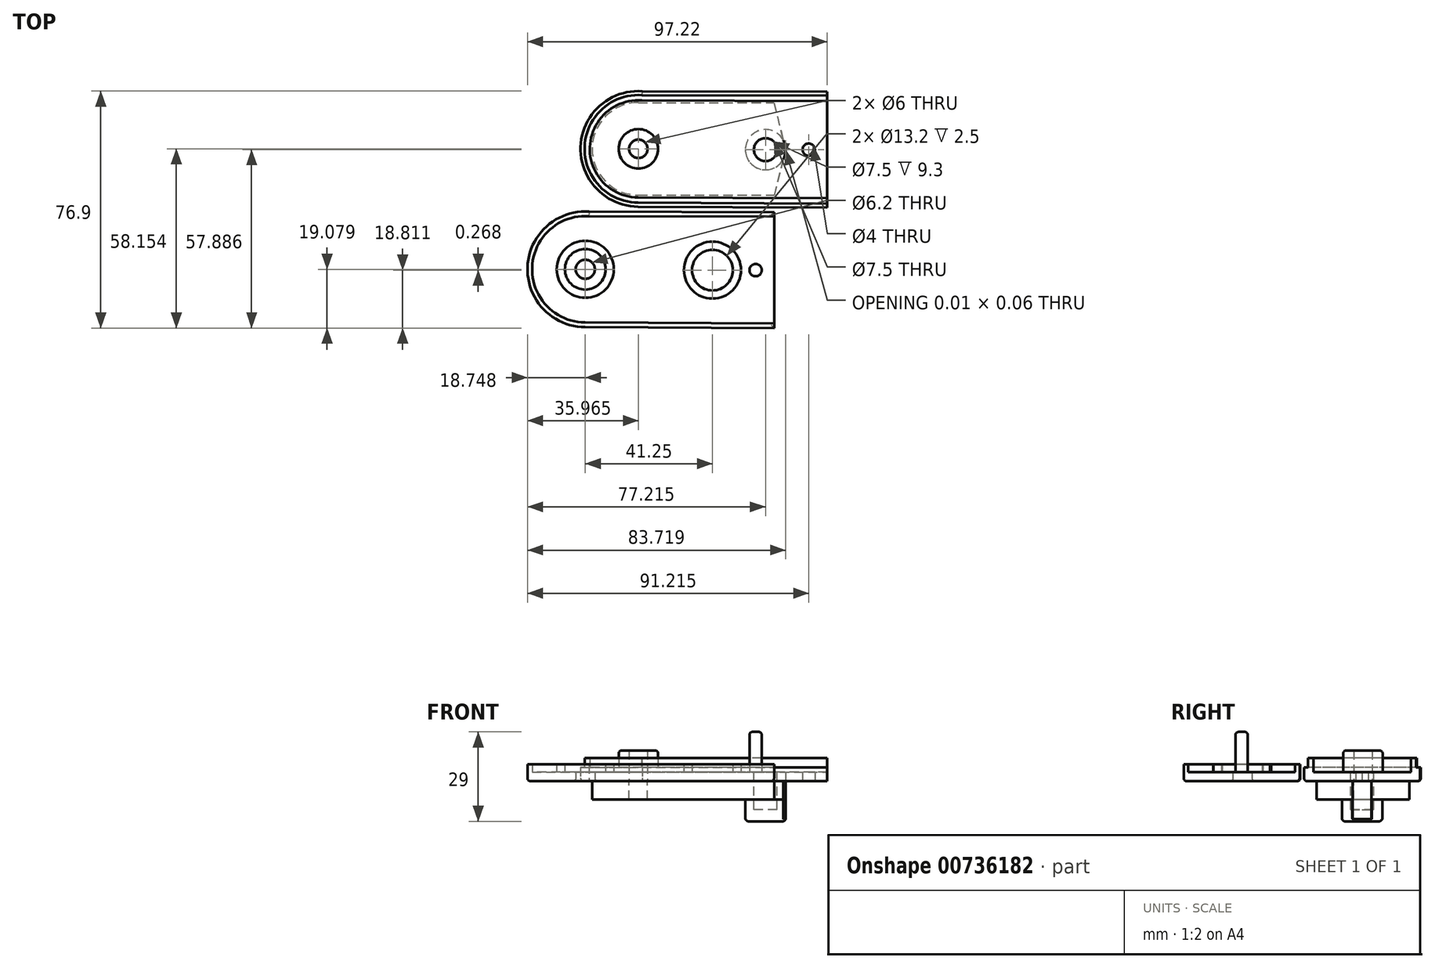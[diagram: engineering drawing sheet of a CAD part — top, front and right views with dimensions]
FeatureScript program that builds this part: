
annotation { "Feature Type Name" : "Feature", "Feature Type Description" : "" }
export const myFeature = defineFeature(function(context is Context, id is Id, definition is map)
    precondition{}
    {
        {
            var Q0;
            Q0=qCreatedBy(makeId("Top.planeOp"),FACE);
            var sketch = newSketch(context, id + "F0", { "sketchPlane" : qUnion([Q0])});
            skArc(sketch, "E0", {"start": v(-10, 58.38) * mm, "mid": v(-29.96, 40.34) * mm, "end": v(-11.32, 20.92) * mm});
            skCircle(sketch, "E1", {"center": v(-11.22, 39.67) * mm, "radius": 6.4 * mm});
            skCircle(sketch, "E2", {"center": v(-11.22, 39.67) * mm, "radius": 3 * mm});
            skLineSegment(sketch, "E3", {"start": v(50.03, 58.21) * mm, "end": v(50.03, 20.6) * mm});
            skLineSegment(sketch, "E4", {"start": v(50.03, 20.6) * mm, "end": v(-11.32, 20.92) * mm});
            skLineSegment(sketch, "E5", {"start": v(-10, 58.38) * mm, "end": v(50.03, 58.21) * mm});
            skCircle(sketch, "E6", {"center": v(30.03, 39.4) * mm, "radius": 4 * mm});
            skCircle(sketch, "E7", {"center": v(44.03, 39.4) * mm, "radius": 2 * mm});
            skArc(sketch, "E8", {"start": v(31.89, 45.64) * mm, "mid": v(23.52, 39.41) * mm, "end": v(31.88, 33.17) * mm});
            skArc(sketch, "E9", {"start": v(-11.27, 54.67) * mm, "mid": v(-26.22, 39.67) * mm, "end": v(-11.27, 24.67) * mm});
            skLineSegment(sketch, "E10.bottom", {"start": v(-11.27, 54.67) * mm, "end": v(32.73, 54.67) * mm});
            skLineSegment(sketch, "E10.top", {"start": v(-11.27, 24.67) * mm, "end": v(32.84, 24.67) * mm});
            skLineSegment(sketch, "E11.0", {"start": v(-10.1, 55.38) * mm, "end": v(50.02, 55.21) * mm});
            skArc(sketch, "E11.1", {"start": v(-10.1, 55.38) * mm, "mid": v(-26.96, 40.28) * mm, "end": v(-11.3, 23.92) * mm});
            skLineSegment(sketch, "E11.2", {"start": v(50.04, 23.6) * mm, "end": v(-11.3, 23.92) * mm});
            skLineSegment(sketch, "E12", {"start": v(32.73, 54.67) * mm, "end": v(35.78, 42.43) * mm});
            skLineSegment(sketch, "E13", {"start": v(36.53, 39.4) * mm, "end": v(36.53, 39.37) * mm});
            skLineSegment(sketch, "E14.0", {"start": v(-11.2, 27.67) * mm, "end": v(30.5, 27.67) * mm});
            skArc(sketch, "E14.1", {"start": v(-11.27, 51.67) * mm, "mid": v(-23.22, 39.64) * mm, "end": v(-11.2, 27.67) * mm});
            skLineSegment(sketch, "E14.2", {"start": v(-11.27, 51.67) * mm, "end": v(30.38, 51.67) * mm});
            skLineSegment(sketch, "E14.3", {"start": v(30.38, 51.67) * mm, "end": v(31.89, 45.64) * mm});
            skLineSegment(sketch, "E14.4", {"start": v(33.44, 39.41) * mm, "end": v(33.44, 39.4) * mm});
            skLineSegment(sketch, "E15.trimOffspring", {"start": v(31.88, 33.17) * mm, "end": v(30.5, 27.67) * mm});
            skLineSegment(sketch, "E16.trimOffspring", {"start": v(-11.27, 24.67) * mm, "end": v(-11.27, 24.67) * mm});
            skLineSegment(sketch, "E17.trimOffspring", {"start": v(-26.22, 39.4) * mm, "end": v(-59.38, 39.4) * mm});
            skPoint(sketch, "E18.start.orphan", {"position": v(50.03, 39.4) * mm});
            skArc(sketch, "E19", {"start": v(35.77, 36.37) * mm, "mid": v(36.53, 39.4) * mm, "end": v(35.78, 42.43) * mm});
            skLineSegment(sketch, "E20.trimOffspring", {"start": v(36.53, 39.44) * mm, "end": v(36.53, 39.4) * mm});
            skLineSegment(sketch, "E21.trimOffspring", {"start": v(35.77, 36.37) * mm, "end": v(32.84, 24.67) * mm});
            skLineSegment(sketch, "E22", {"start": v(50.03, 20.6) * mm, "end": v(50.04, 23.6) * mm});
            skLineSegment(sketch, "E23", {"start": v(50.02, 55.21) * mm, "end": v(50.03, 58.21) * mm});
            skArc(sketch, "E24", {"start": v(-27.21, 19.3) * mm, "mid": v(-47.18, 1.26) * mm, "end": v(-28.54, -18.15) * mm});
            skCircle(sketch, "E25", {"center": v(-28.44, 0.6) * mm, "radius": 6.6 * mm});
            skLineSegment(sketch, "E26", {"start": v(32.8, 19.14) * mm, "end": v(32.8, -18.48) * mm});
            skLineSegment(sketch, "E27", {"start": v(32.8, -18.48) * mm, "end": v(-28.54, -18.15) * mm});
            skLineSegment(sketch, "E28", {"start": v(-27.21, 19.3) * mm, "end": v(32.8, 19.14) * mm});
            skCircle(sketch, "E29", {"center": v(12.8, 0.33) * mm, "radius": 9.25 * mm});
            skCircle(sketch, "E30", {"center": v(26.8, 0.33) * mm, "radius": 2 * mm});
            skLineSegment(sketch, "E31.0", {"start": v(-27.27, 17.8) * mm, "end": v(32.8, 17.64) * mm});
            skArc(sketch, "E31.1", {"start": v(-27.27, 17.8) * mm, "mid": v(-45.68, 1.23) * mm, "end": v(-28.53, -16.65) * mm});
            skLineSegment(sketch, "E31.2", {"start": v(32.81, -16.98) * mm, "end": v(-28.53, -16.65) * mm});
            skLineSegment(sketch, "E32", {"start": v(19.6, 0.26) * mm, "end": v(19.59, 0.23) * mm});
            skLineSegment(sketch, "E33.4", {"start": v(16.22, 0.34) * mm, "end": v(16.22, 0.33) * mm});
            skLineSegment(sketch, "E34.trimOffspring", {"start": v(-28.49, -14.4) * mm, "end": v(-28.49, -14.4) * mm});
            skLineSegment(sketch, "E35.trimOffspring", {"start": v(-43.44, 0.33) * mm, "end": v(-76.6, 0.33) * mm});
            skPoint(sketch, "E36.start.orphan", {"position": v(32.8, 0.33) * mm});
            skLineSegment(sketch, "E37.trimOffspring", {"start": v(19.59, 0.3) * mm, "end": v(19.6, 0.26) * mm});
            skLineSegment(sketch, "E38", {"start": v(32.8, -18.48) * mm, "end": v(32.81, -16.98) * mm});
            skLineSegment(sketch, "E39", {"start": v(32.8, 17.64) * mm, "end": v(32.8, 19.14) * mm});
            skCircle(sketch, "E40", {"center": v(-28.44, 0.6) * mm, "radius": 9.25 * mm});
            skCircle(sketch, "E41", {"center": v(12.8, 0.33) * mm, "radius": 6.6 * mm});
            skCircle(sketch, "E42", {"center": v(-28.44, 0.6) * mm, "radius": 3.1 * mm});
            skSolve(sketch);
        }
        {
            var Q0;
            Q0=makeQuery(id+"F0.imprint","IMPRINT",FACE,{"disambiguationData":[TD([[makeQuery(id+"F0.imprint","IMPRINT",EDGE,{"derivedFrom":sQuery(id+"F0.wireOp",EDGE,"E1")}),-1.0]])]});
            var Q1;
            {var subQ5=sQuery(id+"F0.wireOp",EDGE,"E4");Q1=makeQuery(id+"F0.imprint","IMPRINT",FACE,{"disambiguationData":[TD([[makeQuery(id+"F0.imprint","IMPRINT",EDGE,{"derivedFrom":subQ5}),-1.0]])]});}
            var Q2;
            Q2=makeQuery(id+"F0.imprint","IMPRINT",FACE,{"disambiguationData":[TD([[makeQuery(id+"F0.imprint","IMPRINT",EDGE,{"derivedFrom":sQuery(id+"F0.wireOp",EDGE,"E1")}),1.0]])]});
            var Q3;
            {var subQ0=sQuery(id+"F0.wireOp",EDGE,"E19");var subQ1=sQuery(id+"F0.wireOp",EDGE,"E12");var subQ2=makeQuery(id+"F0.imprint","INTERSECT",VERTEX,{"disambiguationData":[OD(0.0)],"derivedFrom":[subQ1,subQ0]});Q3=makeQuery(id+"F0.imprint","IMPRINT",FACE,{"disambiguationData":[TD([[makeQuery(id+"F0.imprint","IMPRINT",EDGE,{"disambiguationData":[TD([[subQ2,-1.0]])],"derivedFrom":subQ1}),1.0]])]});}
            var Q4;
            Q4=makeQuery(id+"F0.imprint","IMPRINT",FACE,{"disambiguationData":[TD([[makeQuery(id+"F0.imprint","IMPRINT",EDGE,{"derivedFrom":sQuery(id+"F0.wireOp",EDGE,"E8")}),1.0]])]});
            var Q5;
            {var subQ9=sQuery(id+"F0.wireOp",EDGE,"E5");Q5=makeQuery(id+"F0.imprint","IMPRINT",FACE,{"disambiguationData":[TD([[makeQuery(id+"F0.imprint","IMPRINT",EDGE,{"derivedFrom":subQ9}),-1.0]])]});}
            var Q6;
            Q6=makeQuery(id+"F0.imprint","IMPRINT",FACE,{"disambiguationData":[TD([[makeQuery(id+"F0.imprint","IMPRINT",EDGE,{"derivedFrom":sQuery(id+"F0.wireOp",EDGE,"E6")}),1.0]])]});
            extrude(context, id + "F1", {"entities" : qUnion([Q0, Q1, Q2, Q3, Q4, Q5, Q6]), "depth" : 3 * mm, "offsetDistance" : 25 * mm});
        }
        {
            var Q0;
            Q0=makeQuery(id+"F0.imprint","IMPRINT",FACE,{"disambiguationData":[TD([[makeQuery(id+"F0.imprint","IMPRINT",EDGE,{"derivedFrom":sQuery(id+"F0.wireOp",EDGE,"E1")}),-1.0]])]});
            var Q1;
            Q1=makeQuery(id+"F0.imprint","IMPRINT",FACE,{"disambiguationData":[TD([[makeQuery(id+"F0.imprint","IMPRINT",EDGE,{"derivedFrom":sQuery(id+"F0.wireOp",EDGE,"E6")}),-1.0]])]});
            var Q2;
            Q2=makeQuery(id+"F0.imprint","IMPRINT",FACE,{"disambiguationData":[TD([[makeQuery(id+"F0.imprint","IMPRINT",EDGE,{"derivedFrom":sQuery(id+"F0.wireOp",EDGE,"E6")}),1.0]])]});
            var Q3;
            Q3=makeQuery(id+"F0.imprint","IMPRINT",FACE,{"disambiguationData":[TD([[makeQuery(id+"F0.imprint","IMPRINT",EDGE,{"derivedFrom":sQuery(id+"F0.wireOp",EDGE,"E1")}),1.0]])]});
            extrude(context, id + "F2", {"entities" : qUnion([Q0, Q1, Q2, Q3]), "oppositeDirection" : true, "depth" : 6 * mm, "offsetDistance" : 25 * mm});
        }
        {
            var Q0;
            Q0=makeQuery(id+"F2.opExtrude","CAP_FACE",FACE,{"disambiguationData":[OSD([sQuery(id+"F0.wireOp",EDGE,"E2"),sQuery(id+"F0.wireOp",EDGE,"E9"),sQuery(id+"F0.wireOp",EDGE,"E10.bottom"),sQuery(id+"F0.wireOp",EDGE,"E10.top"),sQuery(id+"F0.wireOp",EDGE,"E12"),sQuery(id+"F0.wireOp",EDGE,"E19"),sQuery(id+"F0.wireOp",EDGE,"E21.trimOffspring")])],"isStart":false});
            var sketch = newSketch(context, id + "F3", { "sketchPlane" : qUnion([Q0])});
            skCircle(sketch, "E43", {"center": v(30.03, -39.4) * mm, "radius": 6.54 * mm});
            skSolve(sketch);
        }
        {
            var Q0;
            {var subQ5=makeQuery(id+"F2.opExtrude","CAP_EDGE",EDGE,{"disambiguationData":[OSD([sQuery(id+"F0.wireOp",EDGE,"E19")])],"isStart":false});Q0=makeQuery(id+"F3.imprint","IMPRINT",FACE,{"disambiguationData":[TD([[makeQuery(id+"F3.imprint","IMPRINT",EDGE,{"derivedFrom":subQ5}),-1.0]])]});}
            extrude(context, id + "F4", {"entities" : qUnion([Q0]), "operationType" : NewBodyOperationType.ADD, "depth" : 7 * mm, "offsetDistance" : 25 * mm});
        }
        {
            var Q0;
            Q0=makeQuery(id+"F1.opExtrude","CAP_FACE",FACE,{"disambiguationData":[OSD([sQuery(id+"F0.wireOp",EDGE,"E0"),sQuery(id+"F0.wireOp",EDGE,"E2"),sQuery(id+"F0.wireOp",EDGE,"E3"),sQuery(id+"F0.wireOp",EDGE,"E4"),sQuery(id+"F0.wireOp",EDGE,"E5"),sQuery(id+"F0.wireOp",EDGE,"E7"),sQuery(id+"F0.wireOp",EDGE,"E13"),sQuery(id+"F0.wireOp",EDGE,"E19"),sQuery(id+"F0.wireOp",EDGE,"E20.trimOffspring")])],"isStart":false});
            var sketch = newSketch(context, id + "F5", { "sketchPlane" : qUnion([Q0])});
            skCircle(sketch, "E44.0", {"center": v(-11.22, 39.67) * mm, "radius": 6.4 * mm});
            skSolve(sketch);
        }
        {
            var Q0;
            Q0=makeQuery(id+"F5.imprint","IMPRINT",FACE,{"disambiguationData":[TD([[makeQuery(id+"F5.imprint","IMPRINT",EDGE,{"derivedFrom":sQuery(id+"F5.wireOp",EDGE,"E44.0")}),1.0]])]});
            extrude(context, id + "F6", {"entities" : qUnion([Q0]), "operationType" : NewBodyOperationType.ADD, "depth" : 7 * mm, "offsetDistance" : 25 * mm});
        }
        {
            var Q0;
            {var subQ6=sQuery(id+"F0.wireOp",EDGE,"E5");Q0=makeQuery(id+"F0.imprint","IMPRINT",FACE,{"disambiguationData":[TD([[makeQuery(id+"F0.imprint","IMPRINT",EDGE,{"derivedFrom":subQ6}),-1.0]])]});}
            var Q1;
            {var subQ5=sQuery(id+"F0.wireOp",EDGE,"E4");Q1=makeQuery(id+"F0.imprint","IMPRINT",FACE,{"disambiguationData":[TD([[makeQuery(id+"F0.imprint","IMPRINT",EDGE,{"derivedFrom":subQ5}),-1.0]])]});}
            extrude(context, id + "F7", {"entities" : qUnion([Q0, Q1]), "operationType" : NewBodyOperationType.ADD, "depth" : 7.5 * mm, "offsetDistance" : 25 * mm});
        }
        {
            var Q0;
            Q0=makeQuery(id+"F7.opExtrude","CAP_FACE",FACE,{"disambiguationData":[OSD([sQuery(id+"F0.wireOp",EDGE,"E0"),sQuery(id+"F0.wireOp",EDGE,"E3"),sQuery(id+"F0.wireOp",EDGE,"E4"),sQuery(id+"F0.wireOp",EDGE,"E5"),sQuery(id+"F0.wireOp",EDGE,"E11.0"),sQuery(id+"F0.wireOp",EDGE,"E11.1"),sQuery(id+"F0.wireOp",EDGE,"E11.2"),sQuery(id+"F0.wireOp",EDGE,"E23")])],"isStart":false});
            var sketch = newSketch(context, id + "F8", { "sketchPlane" : qUnion([Q0])});
            skLineSegment(sketch, "E45.0", {"start": v(50.03, 20.6) * mm, "end": v(-11.32, 20.92) * mm});
            skArc(sketch, "E45.1", {"start": v(-10, 58.38) * mm, "mid": v(-29.96, 40.34) * mm, "end": v(-11.32, 20.92) * mm});
            skLineSegment(sketch, "E45.2", {"start": v(-10, 58.38) * mm, "end": v(50.03, 58.21) * mm});
            skPoint(sketch, "E45.3", {"position": v(19.35, 20.76) * mm});
            skLineSegment(sketch, "E46.0", {"start": v(-10.04, 57.08) * mm, "end": v(50.02, 56.91) * mm});
            skArc(sketch, "E46.1", {"start": v(-10.04, 57.08) * mm, "mid": v(-28.66, 40.31) * mm, "end": v(-11.32, 22.22) * mm});
            skLineSegment(sketch, "E46.2", {"start": v(50.03, 21.9) * mm, "end": v(-11.32, 22.22) * mm});
            skLineSegment(sketch, "E47", {"start": v(50.03, 21.9) * mm, "end": v(50.03, 20.6) * mm});
            skLineSegment(sketch, "E48", {"start": v(50.03, 58.21) * mm, "end": v(50.02, 56.91) * mm});
            skSolve(sketch);
        }
        {
            var Q0;
            {var subQ0=sQuery(id+"F8.wireOp",EDGE,"E45.0");Q0=makeQuery(id+"F8.imprint","IMPRINT",FACE,{"disambiguationData":[TD([[makeQuery(id+"F8.imprint","IMPRINT",EDGE,{"derivedFrom":subQ0}),-1.0]])]});}
            extrude(context, id + "F9", {"entities" : qUnion([Q0]), "operationType" : NewBodyOperationType.REMOVE, "oppositeDirection" : true, "depth" : 3 * mm, "offsetDistance" : 25 * mm, "hasSecondDirection" : true, "secondDirectionOppositeDirection" : false, "secondDirectionDepth" : 25 * mm});
        }
        {
            var Q0;
            Q0=makeQuery(id+"F1.opExtrude","CAP_FACE",FACE,{"disambiguationData":[OSD([sQuery(id+"F0.wireOp",EDGE,"E0"),sQuery(id+"F0.wireOp",EDGE,"E2"),sQuery(id+"F0.wireOp",EDGE,"E3"),sQuery(id+"F0.wireOp",EDGE,"E4"),sQuery(id+"F0.wireOp",EDGE,"E5"),sQuery(id+"F0.wireOp",EDGE,"E7"),sQuery(id+"F0.wireOp",EDGE,"E13"),sQuery(id+"F0.wireOp",EDGE,"E19"),sQuery(id+"F0.wireOp",EDGE,"E20.trimOffspring")])],"isStart":false});
            var sketch = newSketch(context, id + "F10", { "sketchPlane" : qUnion([Q0])});
            skCircle(sketch, "E49", {"center": v(30.03, 39.4) * mm, "radius": 3.75 * mm});
            skSolve(sketch);
        }
        {
            var Q0;
            Q0 = qSketchRegion(id + "F10", true);
            extrude(context, id + "F11", {"entities" : qUnion([Q0]), "operationType" : NewBodyOperationType.REMOVE, "oppositeDirection" : true, "depth" : 12.3 * mm, "offsetDistance" : 25 * mm});
        }
        {
            var Q0;
            Q0=makeQuery(id+"F0.imprint","IMPRINT",FACE,{"disambiguationData":[TD([[makeQuery(id+"F0.imprint","IMPRINT",EDGE,{"derivedFrom":sQuery(id+"F0.wireOp",EDGE,"E6")}),1.0]])]});
            var sketch = newSketch(context, id + "F12", { "sketchPlane" : qUnion([Q0])});
            skCircle(sketch, "E50.0", {"center": v(30.03, 39.4) * mm, "radius": 3.75 * mm});
            skSolve(sketch);
        }
        {
            var Q0;
            Q0=makeQuery(id+"F12.imprint","IMPRINT",FACE,{"disambiguationData":[TD([[makeQuery(id+"F12.imprint","IMPRINT",EDGE,{"derivedFrom":sQuery(id+"F12.wireOp",EDGE,"E50.0")}),1.0]])]});
            extrude(context, id + "F13", {"entities" : qUnion([Q0]), "operationType" : NewBodyOperationType.REMOVE, "oppositeDirection" : true, "depth" : 6 * mm, "offsetDistance" : 25 * mm});
        }
        {
            var Q0;
            Q0=makeQuery(id+"F1.opExtrude","CAP_EDGE",EDGE,{"disambiguationData":[OSD([sQuery(id+"F0.wireOp",EDGE,"E4")])],"isStart":true});
            var Q1;
            Q1=makeQuery(id+"F1.opExtrude","CAP_EDGE",EDGE,{"disambiguationData":[OSD([sQuery(id+"F0.wireOp",EDGE,"E0")])],"isStart":true});
            var Q2;
            Q2=makeQuery(id+"F1.opExtrude","CAP_EDGE",EDGE,{"disambiguationData":[OSD([sQuery(id+"F0.wireOp",EDGE,"E5")])],"isStart":true});
            var Q3;
            Q3=makeQuery(id+"F4.opExtrude","CAP_EDGE",EDGE,{"disambiguationData":[OSD([sQuery(id+"F3.wireOp",EDGE,"E43")])],"isStart":false});
            var Q4;
            Q4=makeQuery(id+"F6.opExtrude","CAP_EDGE",EDGE,{"disambiguationData":[OSD([sQuery(id+"F5.wireOp",EDGE,"E44.0")])],"isStart":false});
            fillet(context, id + "F14", {"entities" : qUnion([Q0, Q1, Q2, Q3, Q4]), "radius" : 1 * mm, "tangentPropagation" : true, "allowEdgeOverflow" : false});
        }
        {
            var Q0;
            {var subQ0=sQuery(id+"F0.wireOp",EDGE,"E27");Q0=makeQuery(id+"F0.imprint","IMPRINT",FACE,{"disambiguationData":[TD([[makeQuery(id+"F0.imprint","IMPRINT",EDGE,{"derivedFrom":subQ0}),-1.0]])]});}
            var Q1;
            {var subQ1=sQuery(id+"F0.wireOp",EDGE,"E28");Q1=makeQuery(id+"F0.imprint","IMPRINT",FACE,{"disambiguationData":[TD([[makeQuery(id+"F0.imprint","IMPRINT",EDGE,{"derivedFrom":subQ1}),-1.0]])]});}
            var Q2;
            Q2=makeQuery(id+"F0.imprint","IMPRINT",FACE,{"disambiguationData":[TD([[makeQuery(id+"F0.imprint","IMPRINT",EDGE,{"derivedFrom":sQuery(id+"F0.wireOp",EDGE,"E25")}),-1.0]])]});
            var Q3;
            Q3=makeQuery(id+"F0.imprint","IMPRINT",FACE,{"disambiguationData":[TD([[makeQuery(id+"F0.imprint","IMPRINT",EDGE,{"derivedFrom":sQuery(id+"F0.wireOp",EDGE,"E25")}),1.0]])]});
            var Q4;
            Q4=makeQuery(id+"F0.imprint","IMPRINT",FACE,{"disambiguationData":[TD([[makeQuery(id+"F0.imprint","IMPRINT",EDGE,{"derivedFrom":sQuery(id+"F0.wireOp",EDGE,"E41")}),1.0]])]});
            var Q5;
            Q5=makeQuery(id+"F0.imprint","IMPRINT",FACE,{"disambiguationData":[TD([[makeQuery(id+"F0.imprint","IMPRINT",EDGE,{"derivedFrom":sQuery(id+"F0.wireOp",EDGE,"E29")}),1.0]])]});
            var Q6;
            Q6=makeQuery(id+"F0.imprint","IMPRINT",FACE,{"disambiguationData":[TD([[makeQuery(id+"F0.imprint","IMPRINT",EDGE,{"derivedFrom":sQuery(id+"F0.wireOp",EDGE,"E29")}),-1.0]])]});
            extrude(context, id + "F15", {"entities" : qUnion([Q0, Q1, Q2, Q3, Q4, Q5, Q6]), "depth" : 3 * mm, "offsetDistance" : 25 * mm});
        }
        {
            var Q0;
            {var subQ1=sQuery(id+"F0.wireOp",EDGE,"E28");Q0=makeQuery(id+"F0.imprint","IMPRINT",FACE,{"disambiguationData":[TD([[makeQuery(id+"F0.imprint","IMPRINT",EDGE,{"derivedFrom":subQ1}),-1.0]])]});}
            var Q1;
            {var subQ0=sQuery(id+"F0.wireOp",EDGE,"E27");Q1=makeQuery(id+"F0.imprint","IMPRINT",FACE,{"disambiguationData":[TD([[makeQuery(id+"F0.imprint","IMPRINT",EDGE,{"derivedFrom":subQ0}),-1.0]])]});}
            var Q2;
            Q2=makeQuery(id+"F0.imprint","IMPRINT",FACE,{"disambiguationData":[TD([[makeQuery(id+"F0.imprint","IMPRINT",EDGE,{"derivedFrom":sQuery(id+"F0.wireOp",EDGE,"E29")}),1.0]])]});
            var Q3;
            Q3=makeQuery(id+"F0.imprint","IMPRINT",FACE,{"disambiguationData":[TD([[makeQuery(id+"F0.imprint","IMPRINT",EDGE,{"derivedFrom":sQuery(id+"F0.wireOp",EDGE,"E25")}),-1.0]])]});
            extrude(context, id + "F16", {"entities" : qUnion([Q0, Q1, Q2, Q3]), "operationType" : NewBodyOperationType.ADD, "depth" : 5.5 * mm, "offsetDistance" : 25 * mm});
        }
        {
            var Q0;
            Q0=makeQuery(id+"F0.imprint","IMPRINT",FACE,{"disambiguationData":[TD([[makeQuery(id+"F0.imprint","IMPRINT",EDGE,{"derivedFrom":sQuery(id+"F0.wireOp",EDGE,"E30")}),1.0]])]});
            var Q1;
            Q1=sQuery(id+"F0.wireOp",EDGE,"E30");
            extrude(context, id + "F17", {"entities" : qUnion([Q0]), "operationType" : NewBodyOperationType.ADD, "surfaceEntities" : qUnion([Q1]), "depth" : 16 * mm, "offsetDistance" : 25 * mm});
        }
        {
            var Q0;
            Q0=makeQuery(id+"F17.opExtrude","CAP_EDGE",EDGE,{"disambiguationData":[OSD([sQuery(id+"F0.wireOp",EDGE,"E30")])],"isStart":false});
            var Q1;
            {var subQ0=sQuery(id+"F0.wireOp",EDGE,"E30");Q1=makeQuery(id+"F17.boolean.opBoolean","MERGE",FACE,{"derivedFrom":[makeQuery(id+"F15.opExtrude","CAP_FACE",FACE,{"disambiguationData":[OSD([sQuery(id+"F0.wireOp",EDGE,"E24"),sQuery(id+"F0.wireOp",EDGE,"E26"),sQuery(id+"F0.wireOp",EDGE,"E27"),sQuery(id+"F0.wireOp",EDGE,"E28"),subQ0,sQuery(id+"F0.wireOp",EDGE,"E42")])],"isStart":true}),makeQuery(id+"F17.opExtrude","CAP_FACE",FACE,{"disambiguationData":[OSD([subQ0])],"isStart":true})]});}
            var Q2;
            Q2=makeQuery(id+"F15.opExtrude","CAP_EDGE",EDGE,{"disambiguationData":[OSD([sQuery(id+"F0.wireOp",EDGE,"E30")])],"isStart":false});
            fillet(context, id + "F18", {"entities" : qUnion([Q0, Q1, Q2]), "radius" : 1 * mm, "tangentPropagation" : true, "allowEdgeOverflow" : false});
        }
    });
